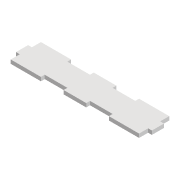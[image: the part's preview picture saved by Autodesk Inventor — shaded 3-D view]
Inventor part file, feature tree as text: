
AUTODESK INVENTOR PART (.ipt)
format: ipt  version: 2022 (Build 260153000, 153)  size: 117,760 bytes
history: native  units: mm
features: extrude x1, sketch x1
ambient origin geometry x8: Origin, YZ Plane, XZ Plane, XY Plane, X Axis, Y Axis, Z Axis, Center Point
bodies: Solid1 (feature_tree)
feature tree (2):
  extrude  "Extrusion1"  Depth=40.0mm
  sketch  "Sketch1"  dims[d0=170.0mm d1=40.0mm d2=5.0mm d3=16.0mm d4=12.0mm d5=5.0mm d6=16.0mm d7=12.0mm d8=5.0mm d9=0.0mm d17=30.0mm d18=5.0mm d19=30.0mm d20=30.0mm d21=15.0mm]
